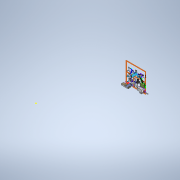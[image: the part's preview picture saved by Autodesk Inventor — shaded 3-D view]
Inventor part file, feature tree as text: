
AUTODESK INVENTOR PART (.ipt)
format: ipt  version: 2022 (Build 260153000, 153)  size: 413,184 bytes
history: native  units: in
note: dims shown in document units (in); Inventor stores cm internally (conversion verified against a paired STEP export)
features: extrude x29, fillet x2, sketch x1
ambient origin geometry x8: Origin, YZ Plane, XZ Plane, XY Plane, X Axis, Y Axis, Z Axis, Center Point
bodies: Solide1 (feature_tree)
feature tree (32):
  sketch  "Esquisse1"
  extrude  "Extrusion1"  Depth=1.9685in TaperAngle=0.0deg
  extrude  "Extrusion2"  Depth=1.5748in TaperAngle=0.0deg
  extrude  "Extrusion3"  Depth=0.7874in TaperAngle=0.0deg
  extrude  "Extrusion4"  Depth=0.3937in
  extrude  "Extrusion5"  Depth=0.3937in
  extrude  "Extrusion6"  Depth=0.3937in
  extrude  "Extrusion10"  Depth=1.5748in TaperAngle=0.0deg
  extrude  "Extrusion12"  Depth=1.5748in TaperAngle=0.0deg
  extrude  "Extrusion13"  Depth=3.937in TaperAngle=0.0deg
  extrude  "Extrusion14"  Depth=0.1181in
  extrude  "Extrusion15"  Depth=0.1181in
  extrude  "Extrusion16"  Depth=1.5748in TaperAngle=0.0deg
  extrude  "Extrusion17"  Depth=2.2835in TaperAngle=0.0deg
  extrude  "Extrusion18"  Depth=0.5906in TaperAngle=0.0deg
  extrude  "Extrusion19"  Depth=0.7874in TaperAngle=0.0deg
  extrude  "Extrusion20"  Depth=0.5906in TaperAngle=0.0deg
  extrude  "Extrusion21"  Depth=0.9921in TaperAngle=0.0deg
  extrude  "Extrusion22"  Depth=0.5906in TaperAngle=0.0deg
  extrude  "Extrusion23"  Depth=0.9921in TaperAngle=0.0deg
  extrude  "Extrusion24"  Depth=2.4646in TaperAngle=0.0deg
  extrude  "Extrusion25"  Depth=0.3937in TaperAngle=0.0deg
  extrude  "Extrusion26"  Depth=4.3307in TaperAngle=0.0deg
  fillet  "Congé1"  Radius=4.3307in
  extrude  "Extrusion27"  Depth=1.1811in TaperAngle=0.0deg
  extrude  "Extrusion28"  Depth=0.9843in TaperAngle=0.0deg
  extrude  "Extrusion29"  Depth=0.3937in
  extrude  "Extrusion30"  Depth=0.3937in
  extrude  "Extrusion31"  Depth=2.0315in TaperAngle=0.0deg
  extrude  "Extrusion32"  Depth=1.3386in TaperAngle=0.0deg
  extrude  "Extrusion33"  Depth=0.5906in
  fillet  "Congé2"  Radius=1.7559in
